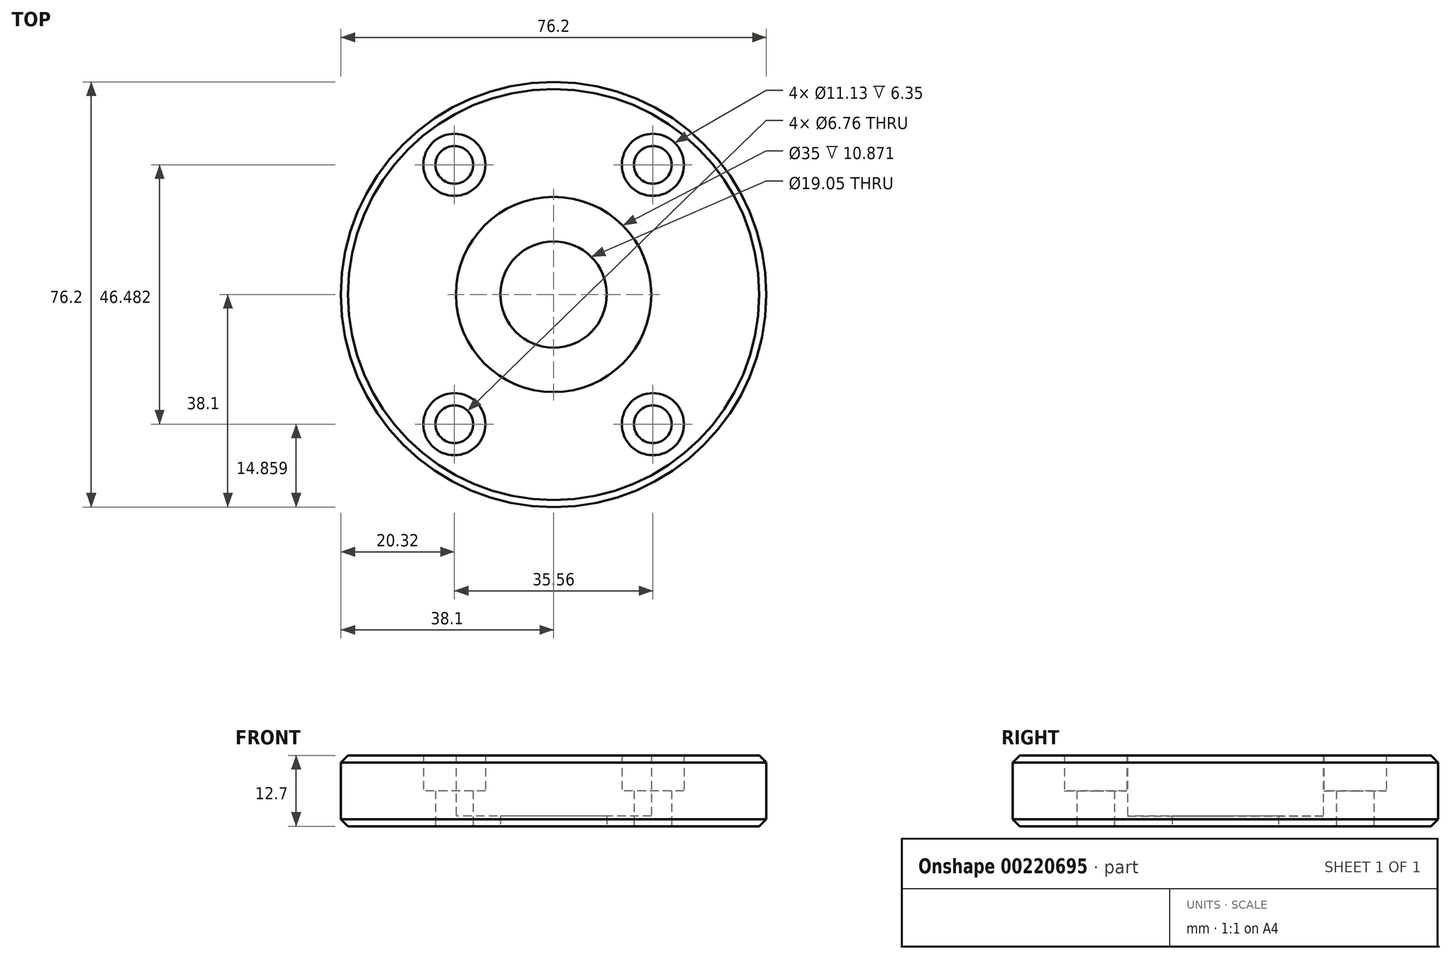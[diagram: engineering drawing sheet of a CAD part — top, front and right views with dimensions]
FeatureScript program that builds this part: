
annotation { "Feature Type Name" : "Feature", "Feature Type Description" : "" }
export const myFeature = defineFeature(function(context is Context, id is Id, definition is map)
    precondition{}
    {
        {
            var Q0;
            Q0=qCreatedBy(makeId("Top.planeOp"),FACE);
            var sketch = newSketch(context, id + "F0", { "sketchPlane" : qUnion([Q0])});
            skCircle(sketch, "E0", {"center": v(0, 0) * mm, "radius": 9.53 * mm});
            skCircle(sketch, "E1", {"center": v(0, 0) * mm, "radius": 38.1 * mm});
            skCircle(sketch, "E2", {"center": v(0, 0) * mm, "radius": 17.5 * mm});
            skCircle(sketch, "E3", {"center": v(17.78, 23.24) * mm, "radius": 5.56 * mm});
            skCircle(sketch, "E4", {"center": v(-17.78, 23.24) * mm, "radius": 5.56 * mm});
            skCircle(sketch, "E5", {"center": v(17.78, -23.24) * mm, "radius": 5.56 * mm});
            skCircle(sketch, "E6", {"center": v(-17.78, -23.24) * mm, "radius": 5.56 * mm});
            skCircle(sketch, "E7", {"center": v(17.78, 23.24) * mm, "radius": 3.38 * mm});
            skCircle(sketch, "E8", {"center": v(-17.78, 23.24) * mm, "radius": 3.38 * mm});
            skCircle(sketch, "E9", {"center": v(17.78, -23.24) * mm, "radius": 3.38 * mm});
            skCircle(sketch, "E10", {"center": v(-17.78, -23.24) * mm, "radius": 3.38 * mm});
            skSolve(sketch);
        }
        {
            var Q0;
            Q0 = qSketchRegion(id + "F0", true);
            extrude(context, id + "F1", {"entities" : qUnion([Q0]), "depth" : 12.7 * mm});
        }
        {
            var Q0;
            Q0=makeQuery(id+"F0.imprint","IMPRINT",FACE,{"disambiguationData":[TD([[makeQuery(id+"F0.imprint","IMPRINT",EDGE,{"derivedFrom":sQuery(id+"F0.wireOp",EDGE,"E4")}),1.0]])]});
            var Q1;
            Q1=makeQuery(id+"F0.imprint","IMPRINT",FACE,{"disambiguationData":[TD([[makeQuery(id+"F0.imprint","IMPRINT",EDGE,{"derivedFrom":sQuery(id+"F0.wireOp",EDGE,"E3")}),1.0]])]});
            var Q2;
            Q2=makeQuery(id+"F0.imprint","IMPRINT",FACE,{"disambiguationData":[TD([[makeQuery(id+"F0.imprint","IMPRINT",EDGE,{"derivedFrom":sQuery(id+"F0.wireOp",EDGE,"E5")}),1.0]])]});
            var Q3;
            Q3=makeQuery(id+"F0.imprint","IMPRINT",FACE,{"disambiguationData":[TD([[makeQuery(id+"F0.imprint","IMPRINT",EDGE,{"derivedFrom":sQuery(id+"F0.wireOp",EDGE,"E6")}),1.0]])]});
            extrude(context, id + "F2", {"entities" : qUnion([Q0, Q1, Q2, Q3]), "operationType" : NewBodyOperationType.ADD, "depth" : 6.35 * mm});
        }
        {
            var Q0;
            Q0=makeQuery(id+"F0.imprint","IMPRINT",FACE,{"disambiguationData":[TD([[makeQuery(id+"F0.imprint","IMPRINT",EDGE,{"derivedFrom":sQuery(id+"F0.wireOp",EDGE,"E0")}),-1.0]])]});
            extrude(context, id + "F3", {"entities" : qUnion([Q0]), "operationType" : NewBodyOperationType.ADD, "depth" : 1.83 * mm});
        }
        {
            var Q0;
            Q0=makeQuery(id+"F1.opExtrude","CAP_EDGE",EDGE,{"disambiguationData":[OSD([sQuery(id+"F0.wireOp",EDGE,"E1")])],"isStart":false});
            var Q1;
            Q1=makeQuery(id+"F1.opExtrude","CAP_EDGE",EDGE,{"disambiguationData":[OSD([sQuery(id+"F0.wireOp",EDGE,"E1")])],"isStart":true});
            chamfer(context, id + "F4", {"entities" : qUnion([Q0, Q1]), "width" : 1.27 * mm, "tangentPropagation" : true});
        }
    });
